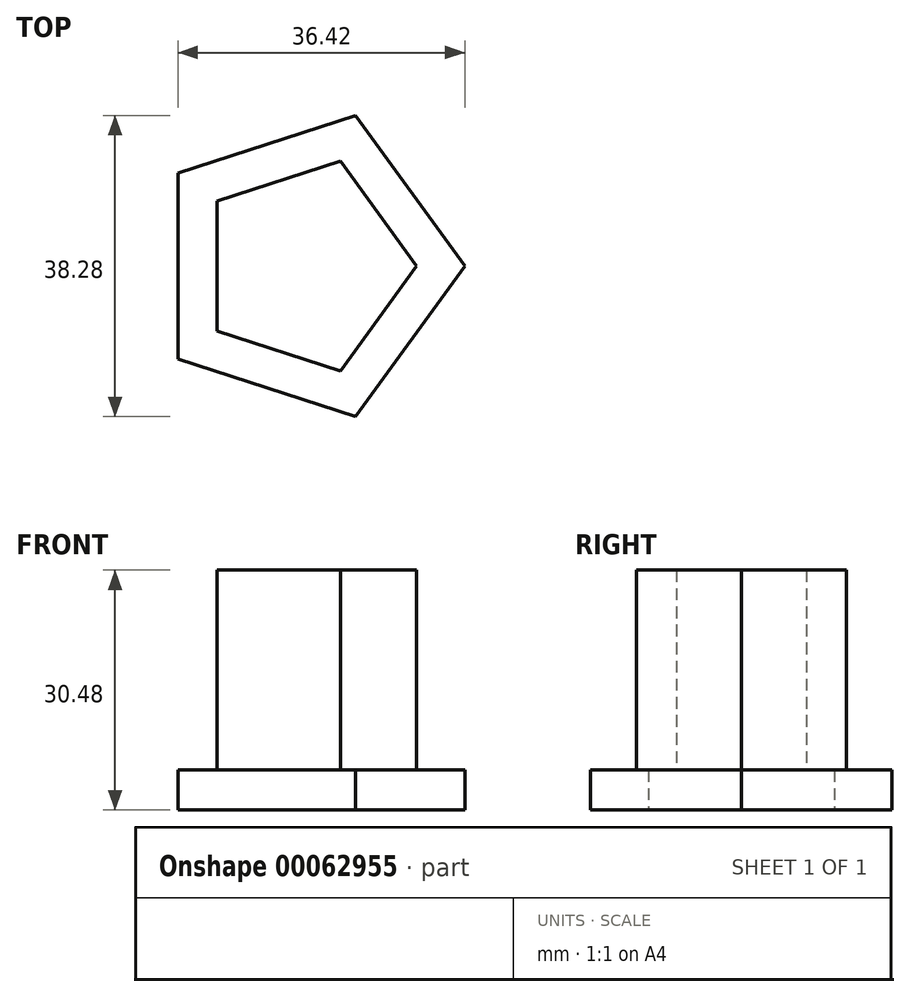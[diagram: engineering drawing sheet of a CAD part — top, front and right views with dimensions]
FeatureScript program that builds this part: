
annotation { "Feature Type Name" : "Feature", "Feature Type Description" : "" }
export const myFeature = defineFeature(function(context is Context, id is Id, definition is map)
    precondition{}
    {
        {
            var Q0;
            Q0=qCreatedBy(makeId("Top.planeOp"),FACE);
            var sketch = newSketch(context, id + "F0", { "sketchPlane" : qUnion([Q0])});
            skCircle(sketch, "E0.cCircle", {"center": v(0, 0) * mm, "radius": 16.29 * mm, "construction": true});
            skLineSegment(sketch, "E0.0", {"start": v(-16.29, -11.83) * mm, "end": v(-16.29, 11.83) * mm});
            skLineSegment(sketch, "E0.1", {"start": v(-16.29, 11.83) * mm, "end": v(6.22, 19.14) * mm});
            skLineSegment(sketch, "E0.2", {"start": v(6.22, 19.14) * mm, "end": v(20.13, 0) * mm});
            skLineSegment(sketch, "E0.3", {"start": v(20.13, 0) * mm, "end": v(6.22, -19.14) * mm});
            skLineSegment(sketch, "E0.4", {"start": v(6.22, -19.14) * mm, "end": v(-16.29, -11.83) * mm});
            skPoint(sketch, "E0.0.midPoint", {"position": v(-16.29, 0) * mm});
            skSolve(sketch);
        }
        {
            var Q0;
            Q0 = qSketchRegion(id + "F0", true);
            extrude(context, id + "F1", {"entities" : qUnion([Q0]), "depth" : 5.08 * mm});
        }
        {
            var Q0;
            Q0=makeQuery(id+"F1.opExtrude","CAP_FACE",FACE,{"disambiguationData":[OSD([sQuery(id+"F0.wireOp",EDGE,"E0.0"),sQuery(id+"F0.wireOp",EDGE,"E0.1"),sQuery(id+"F0.wireOp",EDGE,"E0.2"),sQuery(id+"F0.wireOp",EDGE,"E0.3"),sQuery(id+"F0.wireOp",EDGE,"E0.4")])],"isStart":false});
            var sketch = newSketch(context, id + "F2", { "sketchPlane" : qUnion([Q0])});
            skCircle(sketch, "E1.cCircle", {"center": v(0, 0) * mm, "radius": 11.33 * mm, "construction": true});
            skLineSegment(sketch, "E1.0", {"start": v(-11.33, -8.23) * mm, "end": v(-11.33, 8.23) * mm});
            skLineSegment(sketch, "E1.1", {"start": v(-11.33, 8.23) * mm, "end": v(4.33, 13.32) * mm});
            skLineSegment(sketch, "E1.2", {"start": v(4.33, 13.32) * mm, "end": v(14, 0) * mm});
            skLineSegment(sketch, "E1.3", {"start": v(14, 0) * mm, "end": v(4.33, -13.32) * mm});
            skLineSegment(sketch, "E1.4", {"start": v(4.33, -13.32) * mm, "end": v(-11.33, -8.23) * mm});
            skPoint(sketch, "E1.0.midPoint", {"position": v(-11.33, 0) * mm});
            skSolve(sketch);
        }
        {
            var Q0;
            Q0 = qSketchRegion(id + "F2", true);
            extrude(context, id + "F3", {"entities" : qUnion([Q0]), "operationType" : NewBodyOperationType.ADD, "depth" : 25.4 * mm});
        }
    });
